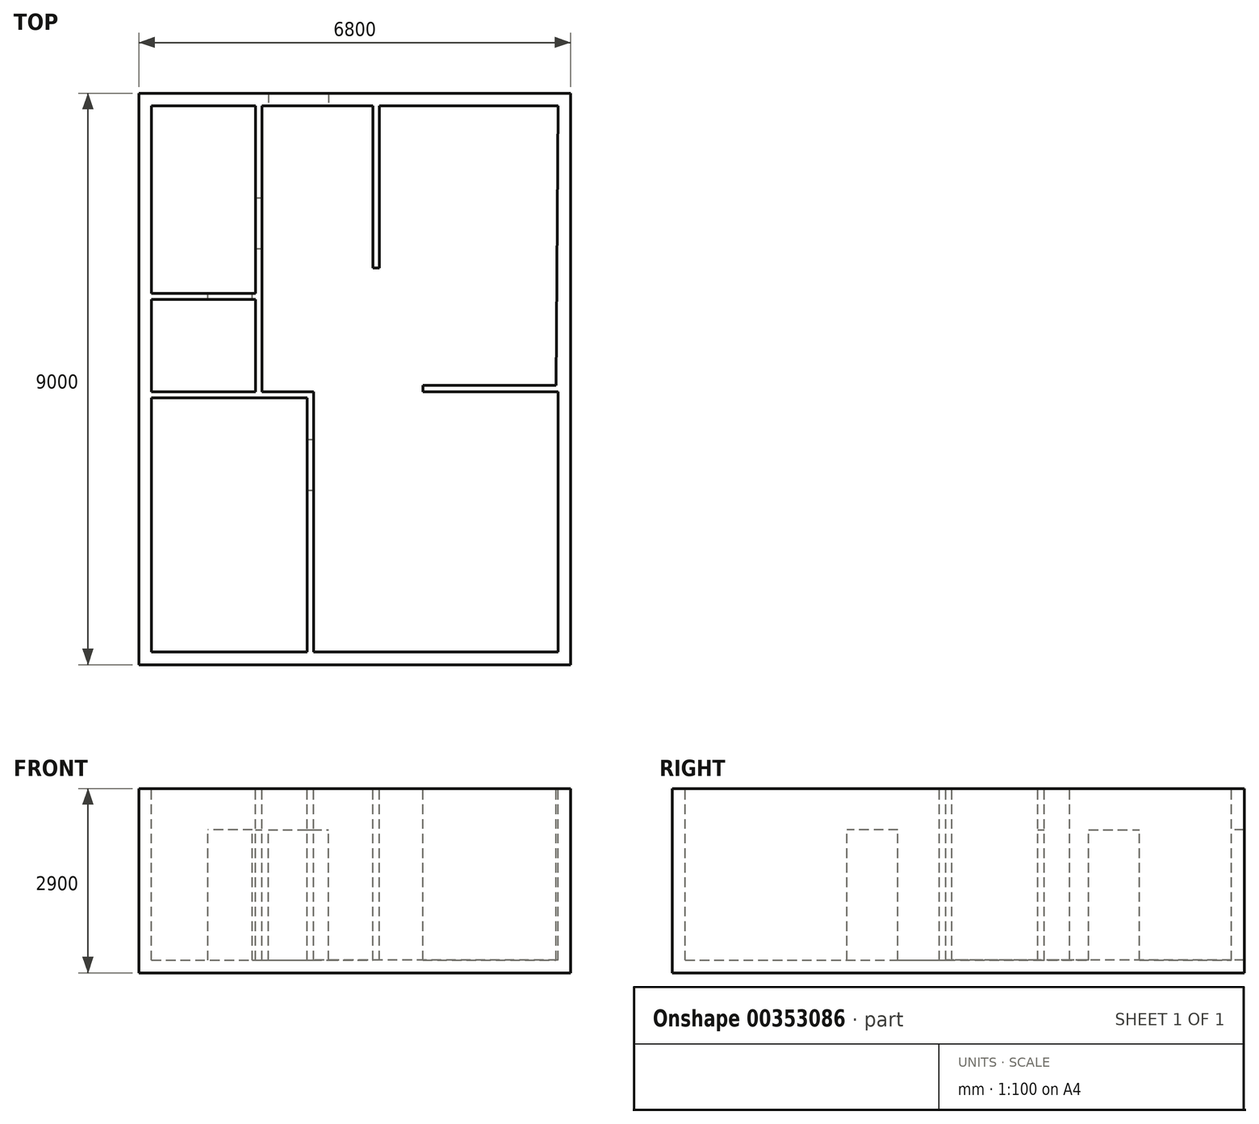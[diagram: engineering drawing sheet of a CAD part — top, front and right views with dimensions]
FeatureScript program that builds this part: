
annotation { "Feature Type Name" : "Feature", "Feature Type Description" : "" }
export const myFeature = defineFeature(function(context is Context, id is Id, definition is map)
    precondition{}
    {
        {
            var Q0;
            Q0=qCreatedBy(makeId("Top.planeOp"),FACE);
            var sketch = newSketch(context, id + "F0", { "sketchPlane" : qUnion([Q0])});
            skLineSegment(sketch, "E0.bottom", {"start": v(-3400, -4500) * mm, "end": v(3400, -4500) * mm});
            skLineSegment(sketch, "E0.top", {"start": v(-3400, 4500) * mm, "end": v(3400, 4500) * mm});
            skLineSegment(sketch, "E0.left", {"start": v(-3400, -4500) * mm, "end": v(-3400, 4500) * mm});
            skLineSegment(sketch, "E0.right", {"start": v(3400, -4500) * mm, "end": v(3400, 4500) * mm});
            skPoint(sketch, "E0.middle", {"position": v(0, 0) * mm});
            skSolve(sketch);
        }
        {
            var Q0;
            Q0 = qSketchRegion(id + "F0", true);
            extrude(context, id + "F1", {"entities" : qUnion([Q0]), "depth" : 2900 * mm});
        }
        {
            var Q0;
            Q0=makeQuery(id+"F1.opExtrude","CAP_FACE",FACE,{"disambiguationData":[OSD([sQuery(id+"F0.wireOp",EDGE,"E0.bottom"),sQuery(id+"F0.wireOp",EDGE,"E0.top"),sQuery(id+"F0.wireOp",EDGE,"E0.left"),sQuery(id+"F0.wireOp",EDGE,"E0.right")])],"isStart":false});
            var sketch = newSketch(context, id + "F2", { "sketchPlane" : qUnion([Q0])});
            skLineSegment(sketch, "E1.bottom", {"start": v(3200, -4300) * mm, "end": v(-650, -4300) * mm});
            skLineSegment(sketch, "E1.top", {"start": v(3200, -200) * mm, "end": v(-650, -200) * mm});
            skLineSegment(sketch, "E1.left", {"start": v(3200, -4300) * mm, "end": v(3200, -200) * mm});
            skLineSegment(sketch, "E1.right", {"start": v(-650, -4300) * mm, "end": v(-650, -200) * mm});
            skSolve(sketch);
        }
        {
            var Q0;
            Q0 = qSketchRegion(id + "F2", true);
            extrude(context, id + "F3", {"entities" : qUnion([Q0]), "operationType" : NewBodyOperationType.REMOVE, "oppositeDirection" : true, "depth" : 2700 * mm});
        }
        {
            var Q0;
            Q0=makeQuery(id+"F1.opExtrude","CAP_FACE",FACE,{"disambiguationData":[OSD([sQuery(id+"F0.wireOp",EDGE,"E0.bottom"),sQuery(id+"F0.wireOp",EDGE,"E0.top"),sQuery(id+"F0.wireOp",EDGE,"E0.left"),sQuery(id+"F0.wireOp",EDGE,"E0.right")])],"isStart":false});
            var sketch = newSketch(context, id + "F4", { "sketchPlane" : qUnion([Q0])});
            skLineSegment(sketch, "E2.bottom", {"start": v(-3200, -4300) * mm, "end": v(-750, -4300) * mm});
            skLineSegment(sketch, "E2.top", {"start": v(-3200, -300) * mm, "end": v(-750, -300) * mm});
            skLineSegment(sketch, "E2.left", {"start": v(-3200, -4300) * mm, "end": v(-3200, -300) * mm});
            skLineSegment(sketch, "E2.right", {"start": v(-750, -4300) * mm, "end": v(-750, -300) * mm});
            skSolve(sketch);
        }
        {
            var Q0;
            Q0 = qSketchRegion(id + "F4", true);
            extrude(context, id + "F5", {"entities" : qUnion([Q0]), "operationType" : NewBodyOperationType.REMOVE, "oppositeDirection" : true, "depth" : 2700 * mm});
        }
        {
            var Q0;
            Q0=makeQuery(id+"F1.opExtrude","CAP_FACE",FACE,{"disambiguationData":[OSD([sQuery(id+"F0.wireOp",EDGE,"E0.bottom"),sQuery(id+"F0.wireOp",EDGE,"E0.top"),sQuery(id+"F0.wireOp",EDGE,"E0.left"),sQuery(id+"F0.wireOp",EDGE,"E0.right")])],"isStart":false});
            var sketch = newSketch(context, id + "F6", { "sketchPlane" : qUnion([Q0])});
            skLineSegment(sketch, "E3.bottom", {"start": v(-1462, -200) * mm, "end": v(288, -200) * mm});
            skLineSegment(sketch, "E3.top", {"start": v(-1462, 4300) * mm, "end": v(288, 4300) * mm});
            skLineSegment(sketch, "E3.left", {"start": v(-1462, -200) * mm, "end": v(-1462, 4300) * mm});
            skLineSegment(sketch, "E3.right", {"start": v(288, -200) * mm, "end": v(288, 4300) * mm});
            skSolve(sketch);
        }
        {
            var Q0;
            Q0 = qSketchRegion(id + "F6", true);
            extrude(context, id + "F7", {"entities" : qUnion([Q0]), "operationType" : NewBodyOperationType.REMOVE, "oppositeDirection" : true, "depth" : 2700 * mm});
        }
        {
            var Q0;
            Q0=makeQuery(id+"F1.opExtrude","CAP_FACE",FACE,{"disambiguationData":[OSD([sQuery(id+"F0.wireOp",EDGE,"E0.bottom"),sQuery(id+"F0.wireOp",EDGE,"E0.top"),sQuery(id+"F0.wireOp",EDGE,"E0.left"),sQuery(id+"F0.wireOp",EDGE,"E0.right")])],"isStart":false});
            var sketch = newSketch(context, id + "F8", { "sketchPlane" : qUnion([Q0])});
            skLineSegment(sketch, "E4.bottom", {"start": v(3200, 4300) * mm, "end": v(388, 4300) * mm});
            skLineSegment(sketch, "E4.left", {"start": v(3200, 4300) * mm, "end": v(3170.17, -100) * mm});
            skLineSegment(sketch, "E5", {"start": v(388, 4300) * mm, "end": v(388, 1750) * mm});
            skLineSegment(sketch, "E6", {"start": v(388, 1750) * mm, "end": v(288, 1750) * mm});
            skLineSegment(sketch, "E7", {"start": v(288, 1750) * mm, "end": v(288, -200) * mm});
            skLineSegment(sketch, "E8", {"start": v(288, -200) * mm, "end": v(1070.17, -200) * mm});
            skLineSegment(sketch, "E9", {"start": v(1070.17, -200) * mm, "end": v(1070.17, -100) * mm});
            skLineSegment(sketch, "E10", {"start": v(1070.17, -100) * mm, "end": v(3170.17, -100) * mm});
            skSolve(sketch);
        }
        {
            var Q0;
            Q0 = qSketchRegion(id + "F8", true);
            extrude(context, id + "F9", {"entities" : qUnion([Q0]), "operationType" : NewBodyOperationType.REMOVE, "oppositeDirection" : true, "depth" : 2700 * mm});
        }
        {
            var Q0;
            Q0=makeQuery(id+"F1.opExtrude","CAP_FACE",FACE,{"disambiguationData":[OSD([sQuery(id+"F0.wireOp",EDGE,"E0.bottom"),sQuery(id+"F0.wireOp",EDGE,"E0.top"),sQuery(id+"F0.wireOp",EDGE,"E0.left"),sQuery(id+"F0.wireOp",EDGE,"E0.right")])],"isStart":false});
            var sketch = newSketch(context, id + "F10", { "sketchPlane" : qUnion([Q0])});
            skLineSegment(sketch, "E11.bottom", {"start": v(-3200, 4300) * mm, "end": v(-1562, 4300) * mm});
            skLineSegment(sketch, "E11.top", {"start": v(-3200, 1350) * mm, "end": v(-1562, 1350) * mm});
            skLineSegment(sketch, "E11.left", {"start": v(-3200, 4300) * mm, "end": v(-3200, 1350) * mm});
            skLineSegment(sketch, "E11.right", {"start": v(-1562, 4300) * mm, "end": v(-1562, 1350) * mm});
            skLineSegment(sketch, "E12.bottom", {"start": v(-3200, 1250) * mm, "end": v(-1562, 1250) * mm});
            skLineSegment(sketch, "E12.top", {"start": v(-3200, -200) * mm, "end": v(-1562, -200) * mm});
            skLineSegment(sketch, "E12.left", {"start": v(-3200, 1250) * mm, "end": v(-3200, -200) * mm});
            skLineSegment(sketch, "E12.right", {"start": v(-1562, 1250) * mm, "end": v(-1562, -200) * mm});
            skSolve(sketch);
        }
        {
            var Q0;
            Q0 = qSketchRegion(id + "F10", true);
            extrude(context, id + "F11", {"entities" : qUnion([Q0]), "operationType" : NewBodyOperationType.REMOVE, "oppositeDirection" : true, "depth" : 2700 * mm});
        }
        {
            var Q0;
            Q0=makeQuery(id+"F3.boolean.opBoolean","COPY",FACE,{"derivedFrom":makeQuery(id+"F3.opExtrude","SWEPT_FACE",FACE,{"disambiguationData":[OSD([sQuery(id+"F2.wireOp",EDGE,"E1.right")])]})});
            var sketch = newSketch(context, id + "F12", { "sketchPlane" : qUnion([Q0])});
            skLineSegment(sketch, "E13.bottom", {"start": v(-950, 200) * mm, "end": v(-1750, 200) * mm});
            skLineSegment(sketch, "E13.top", {"start": v(-950, 2250) * mm, "end": v(-1750, 2250) * mm});
            skLineSegment(sketch, "E13.left", {"start": v(-950, 200) * mm, "end": v(-950, 2250) * mm});
            skLineSegment(sketch, "E13.right", {"start": v(-1750, 200) * mm, "end": v(-1750, 2250) * mm});
            skSolve(sketch);
        }
        {
            var Q0;
            Q0 = qSketchRegion(id + "F12", true);
            extrude(context, id + "F13", {"entities" : qUnion([Q0]), "operationType" : NewBodyOperationType.REMOVE, "oppositeDirection" : true, "depth" : 100 * mm});
        }
        {
            var Q0;
            Q0=makeQuery(id+"F7.boolean.opBoolean","COPY",FACE,{"derivedFrom":makeQuery(id+"F7.opExtrude","SWEPT_FACE",FACE,{"disambiguationData":[OSD([sQuery(id+"F6.wireOp",EDGE,"E3.left")])]})});
            var sketch = newSketch(context, id + "F14", { "sketchPlane" : qUnion([Q0])});
            skLineSegment(sketch, "E14.bottom", {"start": v(2050, 200) * mm, "end": v(2850, 200) * mm});
            skLineSegment(sketch, "E14.top", {"start": v(2050, 2250) * mm, "end": v(2850, 2250) * mm});
            skLineSegment(sketch, "E14.left", {"start": v(2050, 200) * mm, "end": v(2050, 2250) * mm});
            skLineSegment(sketch, "E14.right", {"start": v(2850, 200) * mm, "end": v(2850, 2250) * mm});
            skSolve(sketch);
        }
        {
            var Q0;
            Q0 = qSketchRegion(id + "F14", true);
            extrude(context, id + "F15", {"entities" : qUnion([Q0]), "operationType" : NewBodyOperationType.REMOVE, "oppositeDirection" : true, "depth" : 100 * mm});
        }
        {
            var Q0;
            Q0=makeQuery(id+"F7.boolean.opBoolean","COPY",FACE,{"derivedFrom":makeQuery(id+"F7.opExtrude","SWEPT_FACE",FACE,{"disambiguationData":[OSD([sQuery(id+"F6.wireOp",EDGE,"E3.top")])]})});
            var sketch = newSketch(context, id + "F16", { "sketchPlane" : qUnion([Q0])});
            skLineSegment(sketch, "E15.bottom", {"start": v(-1362, 200) * mm, "end": v(-412, 200) * mm});
            skLineSegment(sketch, "E15.top", {"start": v(-1362, 2250) * mm, "end": v(-412, 2250) * mm});
            skLineSegment(sketch, "E15.left", {"start": v(-1362, 200) * mm, "end": v(-1362, 2250) * mm});
            skLineSegment(sketch, "E15.right", {"start": v(-412, 200) * mm, "end": v(-412, 2250) * mm});
            skSolve(sketch);
        }
        {
            var Q0;
            Q0 = qSketchRegion(id + "F16", true);
            extrude(context, id + "F17", {"entities" : qUnion([Q0]), "operationType" : NewBodyOperationType.REMOVE, "oppositeDirection" : true, "depth" : 200 * mm});
        }
        {
            var Q0;
            Q0=makeQuery(id+"F11.boolean.opBoolean","COPY",FACE,{"derivedFrom":makeQuery(id+"F11.opExtrude","SWEPT_FACE",FACE,{"disambiguationData":[OSD([sQuery(id+"F10.wireOp",EDGE,"E11.top")])]})});
            var sketch = newSketch(context, id + "F18", { "sketchPlane" : qUnion([Q0])});
            skLineSegment(sketch, "E16.bottom", {"start": v(1612, 200) * mm, "end": v(2312, 200) * mm});
            skLineSegment(sketch, "E16.top", {"start": v(1612, 2250) * mm, "end": v(2312, 2250) * mm});
            skLineSegment(sketch, "E16.left", {"start": v(1612, 200) * mm, "end": v(1612, 2250) * mm});
            skLineSegment(sketch, "E16.right", {"start": v(2312, 200) * mm, "end": v(2312, 2250) * mm});
            skSolve(sketch);
        }
        {
            var Q0;
            Q0 = qSketchRegion(id + "F18", true);
            extrude(context, id + "F19", {"entities" : qUnion([Q0]), "operationType" : NewBodyOperationType.REMOVE, "oppositeDirection" : true, "depth" : 100 * mm});
        }
    });
